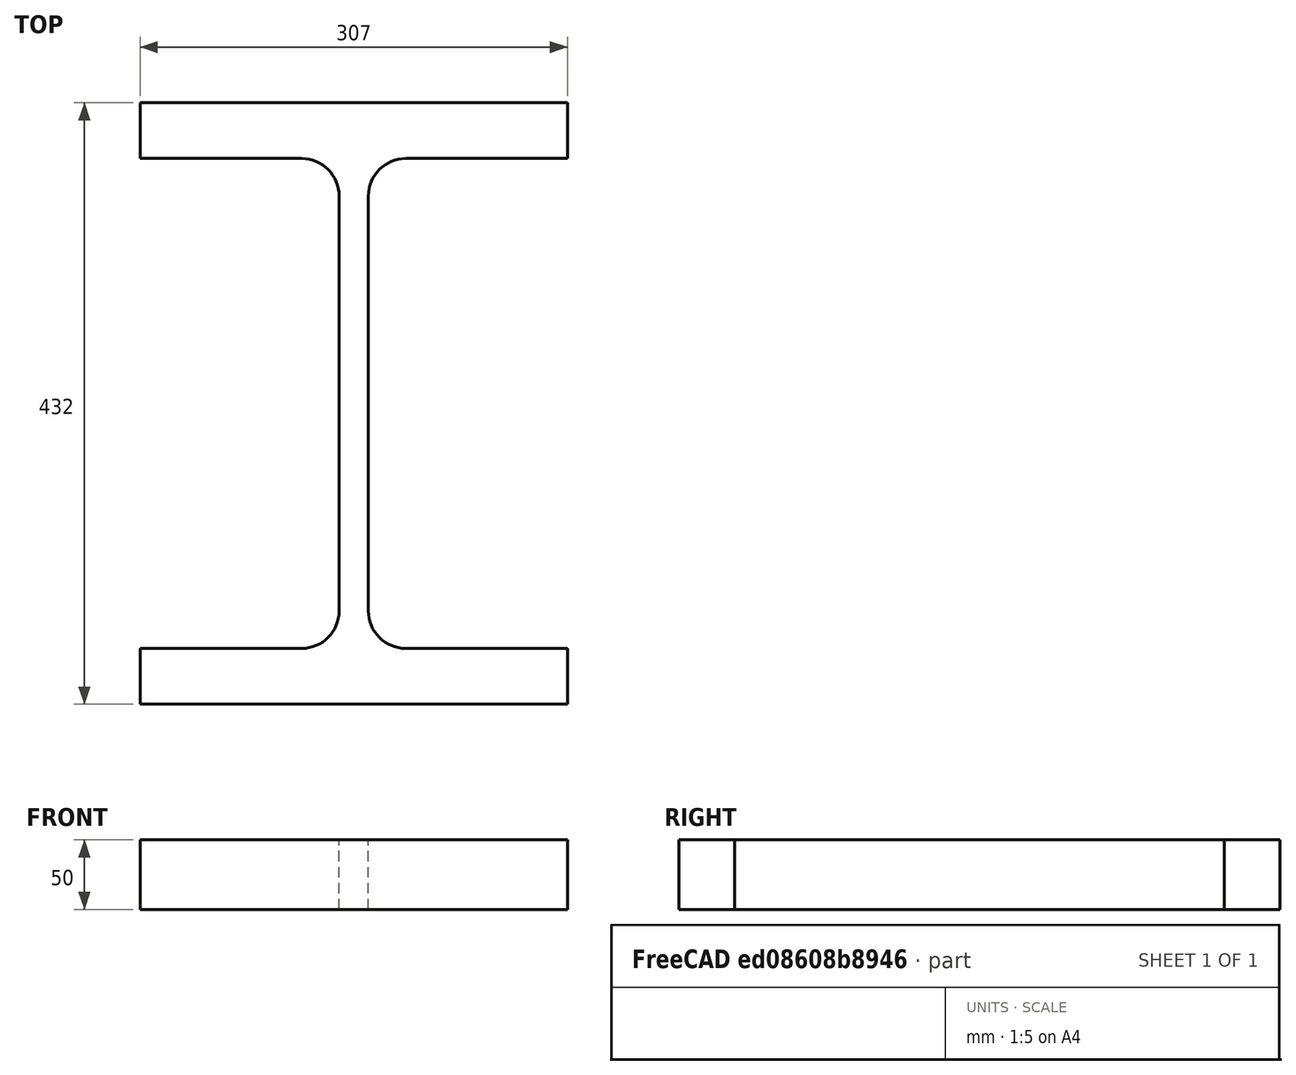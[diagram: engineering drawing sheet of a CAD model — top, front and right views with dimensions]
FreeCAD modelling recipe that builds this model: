
FCSTD DOCUMENT  (FreeCAD 0.15R4671 (Git))
Label: HE-M-Profile 400 DIN1025-4 S235JR
License: All rights reserved
LicenseURL: http://en.wikipedia.org/wiki/All_rights_reserved
objects: Sketcher::SketchObject×1, Part::Extrusion×1
note: 2 computed .brp shape members not serialized (recipe doc carries the construction recipe); baked Part::Feature solids carry a one-line shape summary decoded from their .brp

FEATURE [Sketcher::SketchObject] Sketch
  sketch-geometry (16):
    g0: LineSegment StartX=10.5 StartY=-149 StartZ=0 EndX=10.5 EndY=149 EndZ=0
    g1: LineSegment StartX=37.5 StartY=176 StartZ=0 EndX=153.5 EndY=176 EndZ=0
    g2: LineSegment StartX=153.5 StartY=176 StartZ=0 EndX=153.5 EndY=216 EndZ=0
    g3: LineSegment StartX=153.5 StartY=216 StartZ=0 EndX=-153.5 EndY=216 EndZ=0
    g4: LineSegment StartX=-153.5 StartY=216 StartZ=0 EndX=-153.5 EndY=176 EndZ=0
    g5: LineSegment StartX=-153.5 StartY=176 StartZ=0 EndX=-37.5 EndY=176 EndZ=0
    g6: LineSegment StartX=-10.5 StartY=149 StartZ=0 EndX=-10.5 EndY=-149 EndZ=0
    g7: LineSegment StartX=-37.5 StartY=-176 StartZ=0 EndX=-153.5 EndY=-176 EndZ=0
    g8: LineSegment StartX=-153.5 StartY=-176 StartZ=0 EndX=-153.5 EndY=-216 EndZ=0
    g9: LineSegment StartX=-153.5 StartY=-216 StartZ=0 EndX=153.5 EndY=-216 EndZ=0
    g10: LineSegment StartX=153.5 StartY=-216 StartZ=0 EndX=153.5 EndY=-176 EndZ=0
    g11: LineSegment StartX=153.5 StartY=-176 StartZ=0 EndX=37.5 EndY=-176 EndZ=0
    g12: ArcOfCircle CenterX=37.5 CenterY=149 CenterZ=0 NormalX=0 NormalY=0 NormalZ=1 Radius=27 StartAngle=1.5708 EndAngle=3.14159
    g13: ArcOfCircle CenterX=37.5 CenterY=-149 CenterZ=0 NormalX=0 NormalY=0 NormalZ=1 Radius=27 StartAngle=3.14159 EndAngle=4.71239
    g14: ArcOfCircle CenterX=-37.5 CenterY=149 CenterZ=0 NormalX=0 NormalY=0 NormalZ=1 Radius=27 StartAngle=0 EndAngle=1.5708
    g15: ArcOfCircle CenterX=-37.5 CenterY=-149 CenterZ=0 NormalX=0 NormalY=0 NormalZ=1 Radius=27 StartAngle=4.71239 EndAngle=6.28319
  constraints (42):
    c: Vertical(g0)
    c: Coincident(g2,g1)
    c: Vertical(g2)
    c: Coincident(g3,g2)
    c: Coincident(g4,g3)
    c: Vertical(g4)
    c: Coincident(g5,g4)
    c: Horizontal(g5)
    c: Vertical(g6)
    c: Horizontal(g7)
    c: Coincident(g8,g7)
    c: Vertical(g8)
    c: Coincident(g9,g8)
    c: Horizontal(g9)
    c: Coincident(g10,g9)
    c: Vertical(g10)
    c: Coincident(g11,g10)
    c: Horizontal(g11)
    c: Tangent(g1,g12) = 1.5708
    c: Tangent(g0,g12) = 1.5708
    c: Tangent(g0,g13) = 1.5708
    c: Tangent(g11,g13) = 1.5708
    c: Tangent(g5,g14) = 1.5708
    c: Tangent(g6,g14) = 1.5708
    c: Tangent(g6,g15) = 1.5708
    c: Tangent(g7,g15) = 1.5708
    c: Equal(g3,g9)
    c: Equal(g2,g4)
    c: Equal(g4,g8)
    c: Equal(g8,g10)
    c: Equal(g12,g14)
    c: Equal(g14,g15)
    c: Equal(g15,g13)
    c: Symmetric(g2,g3,g-2)
    c: Symmetric(g9,g8,g-2)
    c: Symmetric(g0,g6,g-2)
    c: Symmetric(g2,g9,g-1)
    c: DistanceY(g2,g9) = -432
    c: DistanceX(g3) = -307
    c: DistanceX(g0,g6) = -21
    c: DistanceY(g2) = 40
    c: Radius(g12) = 27
FEATURE [Part::Extrusion] Extrude  label="HE-M-Profile 400 DIN1025-4 S235JR"
  Base = -> Sketch
  Dir = (0,0,50)
  Solid = true
